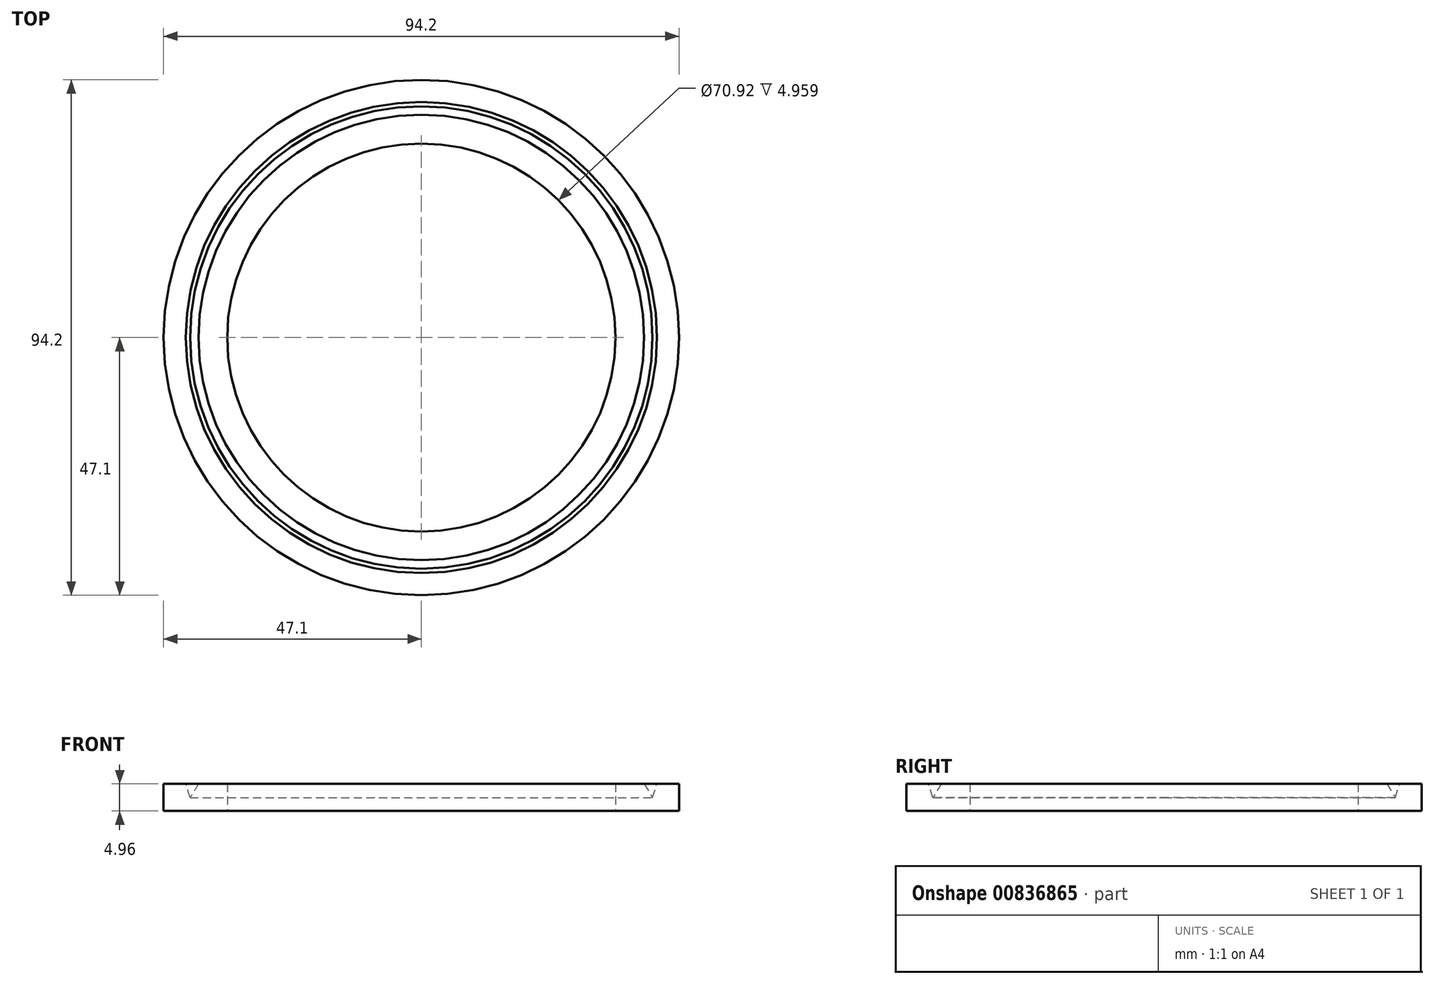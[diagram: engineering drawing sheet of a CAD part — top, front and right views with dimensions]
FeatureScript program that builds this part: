
annotation { "Feature Type Name" : "Feature", "Feature Type Description" : "" }
export const myFeature = defineFeature(function(context is Context, id is Id, definition is map)
    precondition{}
    {
        {
            var Q0;
            Q0=qCreatedBy(makeId("Front.planeOp"),FACE);
            var sketch = newSketch(context, id + "F0", { "sketchPlane" : qUnion([Q0])});
            skLineSegment(sketch, "E0", {"start": v(0, 0) * mm, "end": v(0, 36.44) * mm, "construction": true});
            skLineSegment(sketch, "E1.bottom", {"start": v(35.46, -1.29) * mm, "end": v(47.1, -1.29) * mm});
            skLineSegment(sketch, "E1.top", {"start": v(35.46, -6.25) * mm, "end": v(47.1, -6.25) * mm});
            skLineSegment(sketch, "E1.left", {"start": v(35.46, -1.29) * mm, "end": v(35.46, -6.25) * mm});
            skLineSegment(sketch, "E1.right", {"start": v(47.1, -1.29) * mm, "end": v(47.1, -6.25) * mm});
            skLineSegment(sketch, "E2", {"start": v(70, -57.8) * mm, "end": v(101.58, -29.26) * mm, "construction": true});
            skLineSegment(sketch, "E3", {"start": v(-5.86, -63.28) * mm, "end": v(-39.4, -25.34) * mm, "construction": true});
            skSolve(sketch);
        }
        {
            var Q0;
            Q0=makeQuery(id+"F0.imprint","IMPRINT",FACE,{"disambiguationData":[TD([[makeQuery(id+"F0.imprint","IMPRINT",EDGE,{"derivedFrom":sQuery(id+"F0.wireOp",EDGE,"E1.bottom")}),-1.0]])]});
            var Q1;
            Q1=sQuery(id+"F0.wireOp",EDGE,"E0");
            revolve(context, id + "F1", {"surfaceOperationType" : NewSurfaceOperationType.NEW, "entities" : qUnion([Q0]), "axis" : qUnion([Q1]), "revolveType" : RevolveType.FULL});
        }
        {
            var Q0;
            Q0=qCreatedBy(makeId("Front.planeOp"),FACE);
            var sketch = newSketch(context, id + "F2", { "sketchPlane" : qUnion([Q0])});
            skLineSegment(sketch, "E4", {"start": v(-44.13, 2.1) * mm, "end": v(-42.25, -3.8) * mm});
            skLineSegment(sketch, "E5", {"start": v(-42.25, -3.8) * mm, "end": v(-38.63, 2.1) * mm});
            skLineSegment(sketch, "E6", {"start": v(-38.63, 2.1) * mm, "end": v(-44.13, 2.1) * mm});
            skSolve(sketch);
        }
        {
            var Q0;
            Q0 = qSketchRegion(id + "F2", true);
            var Q1;
            Q1=sQuery(id+"F0.wireOp",EDGE,"E0");
            revolve(context, id + "F3", {"operationType" : NewBodyOperationType.REMOVE, "surfaceOperationType" : NewSurfaceOperationType.NEW, "entities" : qUnion([Q0]), "axis" : qUnion([Q1]), "revolveType" : RevolveType.FULL});
        }
    });
